# Revit family: Legrand Marina version verticale références 036910 à 036950
name_source: partatom
category: Installations électriques
revit_build: Autodesk Revit 2018 (Build: 20170223_1515(x64)
units: mm (PartAtom-declared; Revit-internal decimal feet)

## family parameters
Basée sur le plan de construction = Non
Conserver l'orientation des annotations = Non
Cote de connecteur circulaire = Utiliser le diamètre
Couper avec des vides une fois chargée = Non
Numéro OmniClass = 23.80.00.00
Partagée = Non
Point de calcul de pièce = Non
Titre OmniClass = Electric Power and Lighting
Toujours verticalement = Oui
Type d'élément = Normal

## types (23) — shared parameters
Conditions Générale d'Utilisation = https://export.legrand.com
ETIM Class 6.0 = EC000058
Fabricant = Legrand
IK = 10
IP = 66
Matière = Métal
Nombre de porte = 1
RAL = 7035
URL = www.legrand.fr
Version carrée = Non
Version horizontale = Non
Version verticale = Oui

## per-type parameters (varying)
- Legrand Atlantic 036913: Coffret 036910=Non; Coffret 036912=Non; Coffret 036913=Oui; Coffret 036917=Non; Coffret 036918=Non; Coffret 036919=Non; Coffret 036920=Non; Coffret 036921=Non; Coffret 036925=Non; Coffret 036926=Non; Coffret 036930=Non; Coffret 036931=Non; Coffret 036932=Non; Coffret 036933=Non; Coffret 036937=Non; Coffret 036938=Non; Coffret 036939=Non; Coffret 036942=Non; Coffret 036943=Non; Coffret 036944=Non; Coffret 036945=Non; Coffret 036946=Non; Coffret 036950=Non; Hauteur=500 mm  [stored 1.64042 ft]; Longueur=400 mm  [stored 1.31234 ft]; Poids=9.70 kg; profondeur=160 mm  [stored 0.524934 ft]
- Legrand Atlantic 036920: Coffret 036910=Non; Coffret 036912=Non; Coffret 036913=Non; Coffret 036917=Non; Coffret 036918=Non; Coffret 036919=Non; Coffret 036920=Oui; Coffret 036921=Non; Coffret 036925=Non; Coffret 036926=Non; Coffret 036930=Non; Coffret 036931=Non; Coffret 036932=Non; Coffret 036933=Non; Coffret 036937=Non; Coffret 036938=Non; Coffret 036939=Non; Coffret 036942=Non; Coffret 036943=Non; Coffret 036944=Non; Coffret 036945=Non; Coffret 036946=Non; Coffret 036950=Non; Hauteur=600 mm; Longueur=500 mm  [stored 1.64042 ft]; Poids=16.60 kg; profondeur=200 mm  [stored 0.656168 ft]
- Legrand Atlantic 036921: Coffret 036910=Non; Coffret 036912=Non; Coffret 036913=Non; Coffret 036917=Non; Coffret 036918=Non; Coffret 036919=Non; Coffret 036920=Non; Coffret 036921=Oui; Coffret 036925=Non; Coffret 036926=Non; Coffret 036930=Non; Coffret 036931=Non; Coffret 036932=Non; Coffret 036933=Non; Coffret 036937=Non; Coffret 036938=Non; Coffret 036939=Non; Coffret 036942=Non; Coffret 036943=Non; Coffret 036944=Non; Coffret 036945=Non; Coffret 036946=Non; Coffret 036950=Non; Hauteur=700 mm  [stored 2.29659 ft]; Longueur=500 mm  [stored 1.64042 ft]; Poids=18.40 kg; profondeur=200 mm  [stored 0.656168 ft]
- Legrand Atlantic 036942: Coffret 036910=Non; Coffret 036912=Non; Coffret 036913=Non; Coffret 036917=Non; Coffret 036918=Non; Coffret 036919=Non; Coffret 036920=Non; Coffret 036921=Non; Coffret 036925=Non; Coffret 036926=Non; Coffret 036930=Non; Coffret 036931=Non; Coffret 036932=Non; Coffret 036933=Non; Coffret 036937=Non; Coffret 036938=Non; Coffret 036939=Non; Coffret 036942=Oui; Coffret 036943=Non; Coffret 036944=Non; Coffret 036945=Non; Coffret 036946=Non; Coffret 036950=Non; Hauteur=1200 mm; Longueur=600 mm; Poids=47.00 kg; profondeur=300 mm
- Legrand Atlantic 036910: Coffret 036910=Oui; Coffret 036912=Non; Coffret 036913=Non; Coffret 036917=Non; Coffret 036918=Non; Coffret 036919=Non; Coffret 036920=Non; Coffret 036921=Non; Coffret 036925=Non; Coffret 036926=Non; Coffret 036930=Non; Coffret 036931=Non; Coffret 036932=Non; Coffret 036933=Non; Coffret 036937=Non; Coffret 036938=Non; Coffret 036939=Non; Coffret 036942=Non; Coffret 036943=Non; Coffret 036944=Non; Coffret 036945=Non; Coffret 036946=Non; Coffret 036950=Non; Hauteur=300 mm; Longueur=200 mm  [stored 0.656168 ft]; Poids=3.70 kg; profondeur=160 mm  [stored 0.524934 ft]
- Legrand Atlantic 036912: Coffret 036910=Non; Coffret 036912=Oui; Coffret 036913=Non; Coffret 036917=Non; Coffret 036918=Non; Coffret 036919=Non; Coffret 036920=Non; Coffret 036921=Non; Coffret 036925=Non; Coffret 036926=Non; Coffret 036930=Non; Coffret 036931=Non; Coffret 036932=Non; Coffret 036933=Non; Coffret 036937=Non; Coffret 036938=Non; Coffret 036939=Non; Coffret 036942=Non; Coffret 036943=Non; Coffret 036944=Non; Coffret 036945=Non; Coffret 036946=Non; Coffret 036950=Non; Hauteur=400 mm  [stored 1.31234 ft]; Longueur=300 mm; Poids=6.30 kg; profondeur=160 mm  [stored 0.524934 ft]
- Legrand Atlantic 036917: Coffret 036910=Non; Coffret 036912=Non; Coffret 036913=Non; Coffret 036917=Oui; Coffret 036918=Non; Coffret 036919=Non; Coffret 036920=Non; Coffret 036921=Non; Coffret 036925=Non; Coffret 036926=Non; Coffret 036930=Non; Coffret 036931=Non; Coffret 036932=Non; Coffret 036933=Non; Coffret 036937=Non; Coffret 036938=Non; Coffret 036939=Non; Coffret 036942=Non; Coffret 036943=Non; Coffret 036944=Non; Coffret 036945=Non; Coffret 036946=Non; Coffret 036950=Non; Hauteur=400 mm  [stored 1.31234 ft]; Longueur=300 mm; Poids=6.70 kg; profondeur=200 mm  [stored 0.656168 ft]
- Legrand Atlantic 036918: Coffret 036910=Non; Coffret 036912=Non; Coffret 036913=Non; Coffret 036917=Non; Coffret 036918=Oui; Coffret 036919=Non; Coffret 036920=Non; Coffret 036921=Non; Coffret 036925=Non; Coffret 036926=Non; Coffret 036930=Non; Coffret 036931=Non; Coffret 036932=Non; Coffret 036933=Non; Coffret 036937=Non; Coffret 036938=Non; Coffret 036939=Non; Coffret 036942=Non; Coffret 036943=Non; Coffret 036944=Non; Coffret 036945=Non; Coffret 036946=Non; Coffret 036950=Non; Hauteur=500 mm  [stored 1.64042 ft]; Longueur=400 mm  [stored 1.31234 ft]; Poids=10.60 kg; profondeur=160 mm  [stored 0.524934 ft]
- Legrand Atlantic 036919: Coffret 036910=Non; Coffret 036912=Non; Coffret 036913=Non; Coffret 036917=Non; Coffret 036918=Non; Coffret 036919=Oui; Coffret 036920=Non; Coffret 036921=Non; Coffret 036925=Non; Coffret 036926=Non; Coffret 036930=Non; Coffret 036931=Non; Coffret 036932=Non; Coffret 036933=Non; Coffret 036937=Non; Coffret 036938=Non; Coffret 036939=Non; Coffret 036942=Non; Coffret 036943=Non; Coffret 036944=Non; Coffret 036945=Non; Coffret 036946=Non; Coffret 036950=Non; Hauteur=600 mm; Longueur=400 mm  [stored 1.31234 ft]; Poids=12.00 kg; profondeur=160 mm  [stored 0.524934 ft]
- Legrand Atlantic 036925: Coffret 036910=Non; Coffret 036912=Non; Coffret 036913=Non; Coffret 036917=Non; Coffret 036918=Non; Coffret 036919=Non; Coffret 036920=Non; Coffret 036921=Non; Coffret 036925=Oui; Coffret 036926=Non; Coffret 036930=Non; Coffret 036931=Non; Coffret 036932=Non; Coffret 036933=Non; Coffret 036937=Non; Coffret 036938=Non; Coffret 036939=Non; Coffret 036942=Non; Coffret 036943=Non; Coffret 036944=Non; Coffret 036945=Non; Coffret 036946=Non; Coffret 036950=Non; Hauteur=500 mm  [stored 1.64042 ft]; Longueur=400 mm  [stored 1.31234 ft]; Poids=11.30 kg; profondeur=250 mm  [stored 0.82021 ft]
- Legrand Atlantic 036926: Coffret 036910=Non; Coffret 036912=Non; Coffret 036913=Non; Coffret 036917=Non; Coffret 036918=Non; Coffret 036919=Non; Coffret 036920=Non; Coffret 036921=Non; Coffret 036925=Non; Coffret 036926=Oui; Coffret 036930=Non; Coffret 036931=Non; Coffret 036932=Non; Coffret 036933=Non; Coffret 036937=Non; Coffret 036938=Non; Coffret 036939=Non; Coffret 036942=Non; Coffret 036943=Non; Coffret 036944=Non; Coffret 036945=Non; Coffret 036946=Non; Coffret 036950=Non; Hauteur=500 mm  [stored 1.64042 ft]; Longueur=400 mm  [stored 1.31234 ft]; Poids=12.80 kg; profondeur=250 mm  [stored 0.82021 ft]
- Legrand Atlantic 036930: Coffret 036910=Non; Coffret 036912=Non; Coffret 036913=Non; Coffret 036917=Non; Coffret 036918=Non; Coffret 036919=Non; Coffret 036920=Non; Coffret 036921=Non; Coffret 036925=Non; Coffret 036926=Non; Coffret 036930=Oui; Coffret 036931=Non; Coffret 036932=Non; Coffret 036933=Non; Coffret 036937=Non; Coffret 036938=Non; Coffret 036939=Non; Coffret 036942=Non; Coffret 036943=Non; Coffret 036944=Non; Coffret 036945=Non; Coffret 036946=Non; Coffret 036950=Non; Hauteur=700 mm  [stored 2.29659 ft]; Longueur=500 mm  [stored 1.64042 ft]; Poids=19.60 kg; profondeur=250 mm  [stored 0.82021 ft]
- Legrand Atlantic 036931: Coffret 036910=Non; Coffret 036912=Non; Coffret 036913=Non; Coffret 036917=Non; Coffret 036918=Non; Coffret 036919=Non; Coffret 036920=Non; Coffret 036921=Non; Coffret 036925=Non; Coffret 036926=Non; Coffret 036930=Non; Coffret 036931=Oui; Coffret 036932=Non; Coffret 036933=Non; Coffret 036937=Non; Coffret 036938=Non; Coffret 036939=Non; Coffret 036942=Non; Coffret 036943=Non; Coffret 036944=Non; Coffret 036945=Non; Coffret 036946=Non; Coffret 036950=Non; Hauteur=800 mm  [stored 2.62467 ft]; Longueur=600 mm; Poids=26.60 kg; profondeur=250 mm  [stored 0.82021 ft]
- Legrand Atlantic 036932: Coffret 036910=Non; Coffret 036912=Non; Coffret 036913=Non; Coffret 036917=Non; Coffret 036918=Non; Coffret 036919=Non; Coffret 036920=Non; Coffret 036921=Non; Coffret 036925=Non; Coffret 036926=Non; Coffret 036930=Non; Coffret 036931=Non; Coffret 036932=Oui; Coffret 036933=Non; Coffret 036937=Non; Coffret 036938=Non; Coffret 036939=Non; Coffret 036942=Non; Coffret 036943=Non; Coffret 036944=Non; Coffret 036945=Non; Coffret 036946=Non; Coffret 036950=Non; Hauteur=1000 mm  [stored 3.28084 ft]; Longueur=600 mm; Poids=36.20 kg; profondeur=250 mm  [stored 0.82021 ft]
- Legrand Atlantic 036933: Coffret 036910=Non; Coffret 036912=Non; Coffret 036913=Non; Coffret 036917=Non; Coffret 036918=Non; Coffret 036919=Non; Coffret 036920=Non; Coffret 036921=Non; Coffret 036925=Non; Coffret 036926=Non; Coffret 036930=Non; Coffret 036931=Non; Coffret 036932=Non; Coffret 036933=Oui; Coffret 036937=Non; Coffret 036938=Non; Coffret 036939=Non; Coffret 036942=Non; Coffret 036943=Non; Coffret 036944=Non; Coffret 036945=Non; Coffret 036946=Non; Coffret 036950=Non; Hauteur=1000 mm  [stored 3.28084 ft]; Longueur=800 mm  [stored 2.62467 ft]; Poids=46.80 kg; profondeur=250 mm  [stored 0.82021 ft]
- Legrand Atlantic 036937: Coffret 036910=Non; Coffret 036912=Non; Coffret 036913=Non; Coffret 036917=Non; Coffret 036918=Non; Coffret 036919=Non; Coffret 036920=Non; Coffret 036921=Non; Coffret 036925=Non; Coffret 036926=Non; Coffret 036930=Non; Coffret 036931=Non; Coffret 036932=Non; Coffret 036933=Non; Coffret 036937=Oui; Coffret 036938=Non; Coffret 036939=Non; Coffret 036942=Non; Coffret 036943=Non; Coffret 036944=Non; Coffret 036945=Non; Coffret 036946=Non; Coffret 036950=Non; Hauteur=800 mm  [stored 2.62467 ft]; Longueur=600 mm; Poids=28.80 kg; profondeur=300 mm
- Legrand Atlantic 036938: Coffret 036910=Non; Coffret 036912=Non; Coffret 036913=Non; Coffret 036917=Non; Coffret 036918=Non; Coffret 036919=Non; Coffret 036920=Non; Coffret 036921=Non; Coffret 036925=Non; Coffret 036926=Non; Coffret 036930=Non; Coffret 036931=Non; Coffret 036932=Non; Coffret 036933=Non; Coffret 036937=Non; Coffret 036938=Oui; Coffret 036939=Non; Coffret 036942=Non; Coffret 036943=Non; Coffret 036944=Non; Coffret 036945=Non; Coffret 036946=Non; Coffret 036950=Non; Hauteur=1000 mm  [stored 3.28084 ft]; Longueur=600 mm; Poids=37.80 kg; profondeur=300 mm
- Legrand Atlantic 036939: Coffret 036910=Non; Coffret 036912=Non; Coffret 036913=Non; Coffret 036917=Non; Coffret 036918=Non; Coffret 036919=Non; Coffret 036920=Non; Coffret 036921=Non; Coffret 036925=Non; Coffret 036926=Non; Coffret 036930=Non; Coffret 036931=Non; Coffret 036932=Non; Coffret 036933=Non; Coffret 036937=Non; Coffret 036938=Non; Coffret 036939=Oui; Coffret 036942=Non; Coffret 036943=Non; Coffret 036944=Non; Coffret 036945=Non; Coffret 036946=Non; Coffret 036950=Non; Hauteur=1000 mm  [stored 3.28084 ft]; Longueur=800 mm  [stored 2.62467 ft]; Poids=50.50 kg; profondeur=300 mm
- Legrand Atlantic 036943: Coffret 036910=Non; Coffret 036912=Non; Coffret 036913=Non; Coffret 036917=Non; Coffret 036918=Non; Coffret 036919=Non; Coffret 036920=Non; Coffret 036921=Non; Coffret 036925=Non; Coffret 036926=Non; Coffret 036930=Non; Coffret 036931=Non; Coffret 036932=Non; Coffret 036933=Non; Coffret 036937=Non; Coffret 036938=Non; Coffret 036939=Non; Coffret 036942=Non; Coffret 036943=Oui; Coffret 036944=Non; Coffret 036945=Non; Coffret 036946=Non; Coffret 036950=Non; Hauteur=1200 mm; Longueur=800 mm  [stored 2.62467 ft]; Poids=62.20 kg; profondeur=300 mm
- Legrand Atlantic 036944: Coffret 036910=Non; Coffret 036912=Non; Coffret 036913=Non; Coffret 036917=Non; Coffret 036918=Non; Coffret 036919=Non; Coffret 036920=Non; Coffret 036921=Non; Coffret 036925=Non; Coffret 036926=Non; Coffret 036930=Non; Coffret 036931=Non; Coffret 036932=Non; Coffret 036933=Non; Coffret 036937=Non; Coffret 036938=Non; Coffret 036939=Non; Coffret 036942=Non; Coffret 036943=Non; Coffret 036944=Oui; Coffret 036945=Non; Coffret 036946=Non; Coffret 036950=Non; Hauteur=800 mm  [stored 2.62467 ft]; Longueur=600 mm; Poids=36.80 kg; profondeur=400 mm  [stored 1.31234 ft]
- Legrand Atlantic 036945: Coffret 036910=Non; Coffret 036912=Non; Coffret 036913=Non; Coffret 036917=Non; Coffret 036918=Non; Coffret 036919=Non; Coffret 036920=Non; Coffret 036921=Non; Coffret 036925=Non; Coffret 036926=Non; Coffret 036930=Non; Coffret 036931=Non; Coffret 036932=Non; Coffret 036933=Non; Coffret 036937=Non; Coffret 036938=Non; Coffret 036939=Non; Coffret 036942=Non; Coffret 036943=Non; Coffret 036944=Non; Coffret 036945=Oui; Coffret 036946=Non; Coffret 036950=Non; Hauteur=1000 mm  [stored 3.28084 ft]; Longueur=800 mm  [stored 2.62467 ft]; Poids=62.30 kg; profondeur=400 mm  [stored 1.31234 ft]
- Legrand Atlantic 036946: Coffret 036910=Non; Coffret 036912=Non; Coffret 036913=Non; Coffret 036917=Non; Coffret 036918=Non; Coffret 036919=Non; Coffret 036920=Non; Coffret 036921=Non; Coffret 036925=Non; Coffret 036926=Non; Coffret 036930=Non; Coffret 036931=Non; Coffret 036932=Non; Coffret 036933=Non; Coffret 036937=Non; Coffret 036938=Non; Coffret 036939=Non; Coffret 036942=Non; Coffret 036943=Non; Coffret 036944=Non; Coffret 036945=Non; Coffret 036946=Oui; Coffret 036950=Non; Hauteur=1200 mm; Longueur=800 mm  [stored 2.62467 ft]; Poids=76.00 kg; profondeur=400 mm  [stored 1.31234 ft]
- Legrand Atlantic 036950: Coffret 036910=Non; Coffret 036912=Non; Coffret 036913=Non; Coffret 036917=Non; Coffret 036918=Non; Coffret 036919=Non; Coffret 036920=Non; Coffret 036921=Non; Coffret 036925=Non; Coffret 036926=Non; Coffret 036930=Non; Coffret 036931=Non; Coffret 036932=Non; Coffret 036933=Non; Coffret 036937=Non; Coffret 036938=Non; Coffret 036939=Non; Coffret 036942=Non; Coffret 036943=Non; Coffret 036944=Non; Coffret 036945=Non; Coffret 036946=Non; Coffret 036950=Oui; Hauteur=1400 mm  [stored 4.59318 ft]; Longueur=800 mm  [stored 2.62467 ft]; Poids=80.90 kg; profondeur=400 mm  [stored 1.31234 ft]

note: column(s) folded — value = type name in every type: Description

note: [stored X ft] marks values corroborated as IEEE doubles in the binary element streams (Revit-internal decimal feet)
